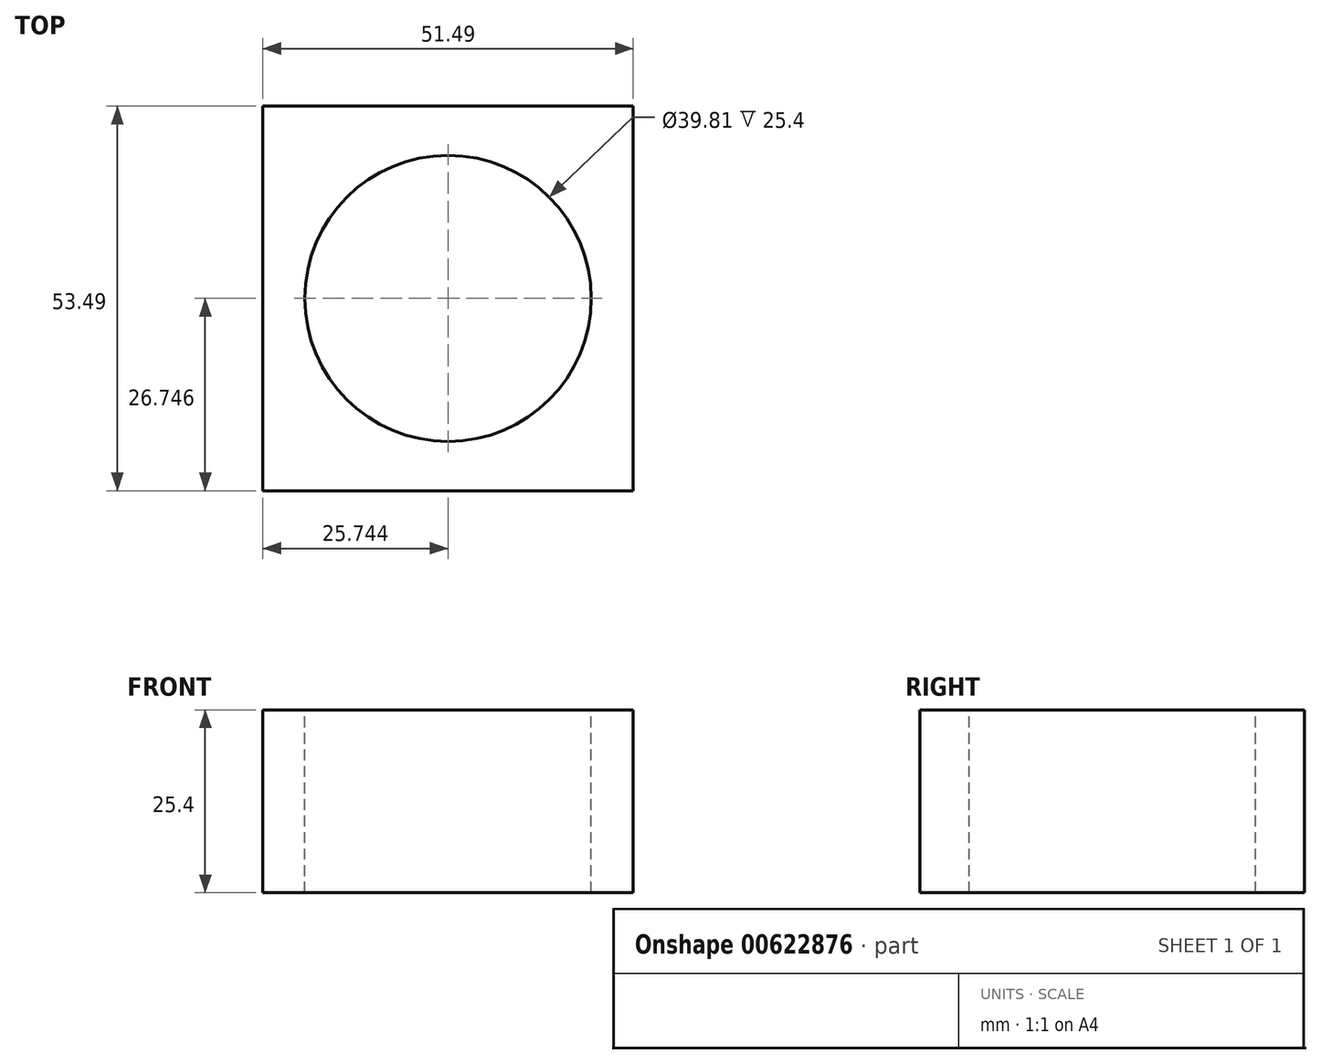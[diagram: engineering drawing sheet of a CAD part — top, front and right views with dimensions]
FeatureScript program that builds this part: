
annotation { "Feature Type Name" : "Feature", "Feature Type Description" : "" }
export const myFeature = defineFeature(function(context is Context, id is Id, definition is map)
    precondition{}
    {
        {
            var Q0;
            Q0=qCreatedBy(makeId("Top.planeOp"),FACE);
            var sketch = newSketch(context, id + "F0", { "sketchPlane" : qUnion([Q0])});
            skLineSegment(sketch, "E0.bottom", {"start": v(0, 0) * mm, "end": v(51.49, 0) * mm});
            skLineSegment(sketch, "E0.top", {"start": v(0, 53.5) * mm, "end": v(51.49, 53.5) * mm});
            skLineSegment(sketch, "E0.left", {"start": v(0, 0) * mm, "end": v(0, 53.5) * mm});
            skLineSegment(sketch, "E0.right", {"start": v(51.49, 0) * mm, "end": v(51.49, 53.5) * mm});
            skSolve(sketch);
        }
        {
            var Q0;
            Q0=makeQuery(id+"F0.imprint","IMPRINT",FACE,{"disambiguationData":[TD([[makeQuery(id+"F0.imprint","IMPRINT",EDGE,{"derivedFrom":sQuery(id+"F0.wireOp",EDGE,"E0.bottom")}),1.0]])]});
            extrude(context, id + "F1", {"entities" : qUnion([Q0]), "depth" : 25.4 * mm, "offsetDistance" : 25.4 * mm});
        }
        {
            var Q0;
            Q0=makeQuery(id+"F1.opExtrude","CAP_FACE",FACE,{"disambiguationData":[OSD([sQuery(id+"F0.wireOp",EDGE,"E0.bottom"),sQuery(id+"F0.wireOp",EDGE,"E0.top"),sQuery(id+"F0.wireOp",EDGE,"E0.left"),sQuery(id+"F0.wireOp",EDGE,"E0.right")])],"isStart":false});
            var sketch = newSketch(context, id + "F2", { "sketchPlane" : qUnion([Q0])});
            skLineSegment(sketch, "E1", {"start": v(0, 26.75) * mm, "end": v(51.49, 26.75) * mm, "construction": true});
            skCircle(sketch, "E2", {"center": v(25.74, 26.75) * mm, "radius": 19.9 * mm});
            skSolve(sketch);
        }
        {
            var Q0;
            Q0=makeQuery(id+"F2.imprint","IMPRINT",FACE,{"disambiguationData":[TD([[makeQuery(id+"F2.imprint","IMPRINT",EDGE,{"derivedFrom":sQuery(id+"F2.wireOp",EDGE,"E2")}),1.0]])]});
            var Q1;
            Q1=sQuery(id+"F2.wireOp",EDGE,"E2");
            extrude(context, id + "F3", {"entities" : qUnion([Q0]), "operationType" : NewBodyOperationType.REMOVE, "surfaceEntities" : qUnion([Q1]), "oppositeDirection" : true, "depth" : 25.4 * mm, "offsetDistance" : 25.4 * mm});
        }
    });
